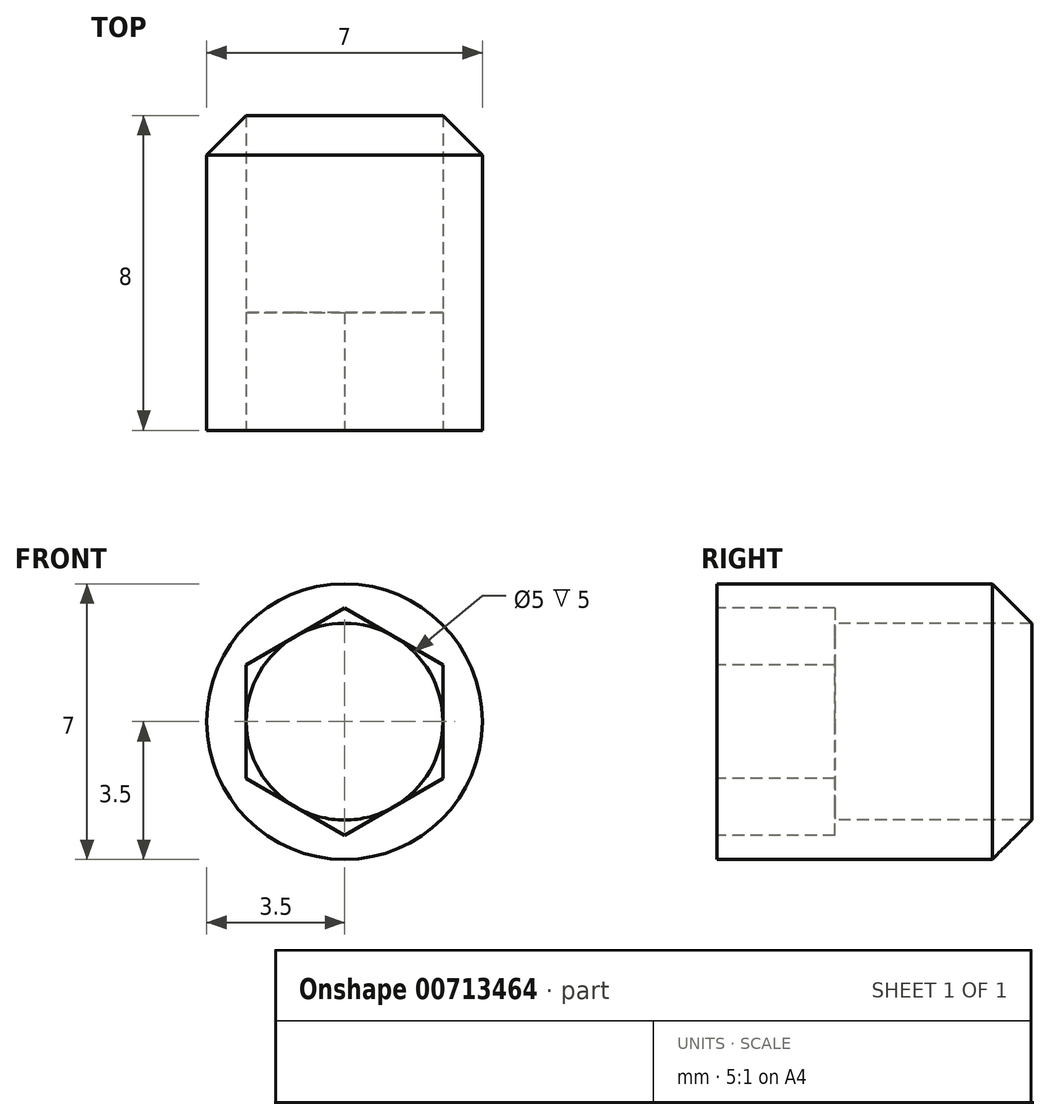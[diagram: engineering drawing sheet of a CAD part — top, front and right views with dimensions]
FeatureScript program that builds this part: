
annotation { "Feature Type Name" : "Feature", "Feature Type Description" : "" }
export const myFeature = defineFeature(function(context is Context, id is Id, definition is map)
    precondition{}
    {
        {
            var Q0;
            Q0=qCreatedBy(makeId("Front.planeOp"),FACE);
            var sketch = newSketch(context, id + "F0", { "sketchPlane" : qUnion([Q0])});
            skCircle(sketch, "E0", {"center": v(0, 0) * mm, "radius": 3.5 * mm});
            skSolve(sketch);
        }
        {
            var Q0;
            Q0=qSketchRegion(id+"F0",true);
            extrude(context, id + "F1", {"entities" : qUnion([Q0]), "depth" : 8 * mm, "offsetDistance" : 25 * mm});
        }
        {
            var Q0;
            Q0=makeQuery(id+"F1.opExtrude","CAP_FACE",FACE,{"disambiguationData":[OSD([sQuery(id+"F0.wireOp",EDGE,"E0")])],"isStart":false});
            var sketch = newSketch(context, id + "F2", { "sketchPlane" : qUnion([Q0])});
            skCircle(sketch, "E1.cCircle", {"center": v(0, 0) * mm, "radius": 2.5 * mm, "construction": true});
            skLineSegment(sketch, "E1.0", {"start": v(0, 2.89) * mm, "end": v(2.5, 1.44) * mm});
            skLineSegment(sketch, "E1.1", {"start": v(2.5, 1.44) * mm, "end": v(2.5, -1.44) * mm});
            skLineSegment(sketch, "E1.2", {"start": v(2.5, -1.44) * mm, "end": v(0, -2.89) * mm});
            skLineSegment(sketch, "E1.3", {"start": v(0, -2.89) * mm, "end": v(-2.5, -1.44) * mm});
            skLineSegment(sketch, "E1.4", {"start": v(-2.5, -1.44) * mm, "end": v(-2.5, 1.44) * mm});
            skLineSegment(sketch, "E1.5", {"start": v(-2.5, 1.44) * mm, "end": v(0, 2.89) * mm});
            skPoint(sketch, "E1.0.midPoint", {"position": v(1.25, 2.17) * mm});
            skSolve(sketch);
        }
        {
            var Q0;
            Q0=qSketchRegion(id+"F2",true);
            extrude(context, id + "F3", {"entities" : qUnion([Q0]), "operationType" : NewBodyOperationType.REMOVE, "oppositeDirection" : true, "depth" : 3 * mm, "offsetDistance" : 25 * mm});
        }
        {
            var Q0;
            Q0=makeQuery(id+"F3.boolean.opBoolean","COPY",FACE,{"derivedFrom":makeQuery(id+"F3.opExtrude","CAP_FACE",FACE,{"disambiguationData":[OSD([sQuery(id+"F2.wireOp",EDGE,"E1.0"),sQuery(id+"F2.wireOp",EDGE,"E1.1"),sQuery(id+"F2.wireOp",EDGE,"E1.2"),sQuery(id+"F2.wireOp",EDGE,"E1.3"),sQuery(id+"F2.wireOp",EDGE,"E1.4"),sQuery(id+"F2.wireOp",EDGE,"E1.5")])],"isStart":false})});
            var sketch = newSketch(context, id + "F4", { "sketchPlane" : qUnion([Q0])});
            skCircle(sketch, "E2", {"center": v(0, 0) * mm, "radius": 2.5 * mm});
            skSolve(sketch);
        }
        {
            var Q0;
            Q0=qSketchRegion(id+"F4",true);
            extrude(context, id + "F5", {"entities" : qUnion([Q0]), "operationType" : NewBodyOperationType.REMOVE, "oppositeDirection" : true, "depth" : 25 * mm, "offsetDistance" : 25 * mm});
        }
        {
            var Q0;
            Q0=makeQuery(id+"F1.opExtrude","CAP_EDGE",EDGE,{"disambiguationData":[OSD([sQuery(id+"F0.wireOp",EDGE,"E0")])],"isStart":true});
            chamfer(context, id + "F6", {"entities" : qUnion([Q0]), "width" : 1 * mm, "tangentPropagation" : true});
        }
    });
